# Revit family: Drain-Trench_MultiDrain_EconoDrain-12-PT2
name_source: partatom
category: Site
units: mm (PartAtom-declared; Revit-internal decimal feet)

## family parameters
Classification Number = 23.10.10.12
Cut with Voids When Loaded = No
Host = Face
Part Type = Normal
Round Connector Dimension = Use Diameter
Shared = No

## types (1)
- Drain-Trench_MultiDrain_EconoDrain-12-PT2
    Assembly Code = A1030600
    Construction Details = http://www.arcat.com
    Default Elevation = 0' - 0"
    Description = MultiDrain Product as Specified
    Expected Lifespan (Years) = 0
    Grate Opening Width = 1' - 2 3/16"
    Keynote = 02600
    Maintenance Schedule (Months) = 0
    Manufacturer = MultiDrain Systems
    Manufacturer Fax = 704-508-1011
    Manufacturer Website = http://www.multidrainsystems.com
    Maximum Run = 0' - 0"
    Model = As Specified
    Piping_Water Flow = 0 GPM
    Product Data = http://www.arcat.com
    Revision = R1_12_2013
    Sales Information = http://www.multidrainsystems.com
    Send Message = http://www.arcat.com
    Specification = http://www.arcat.com
    Trench Width = 0' - 11 15/16"
    URL = http://www.multidrainsystems.com
    Unit Width = 0' - 0"
    Uphill Trench Depth_Maximum = 0' - 8 1/2"
    Uphill Trench Depth_Minimum = 0' - 8"
    Warranty Duration (Years) = 0
    trenchrad = 0' - 5 31/32"

## geometry (parser evidence)
native form markers: Sweep x5
no freeform markers — native parametric forms only
